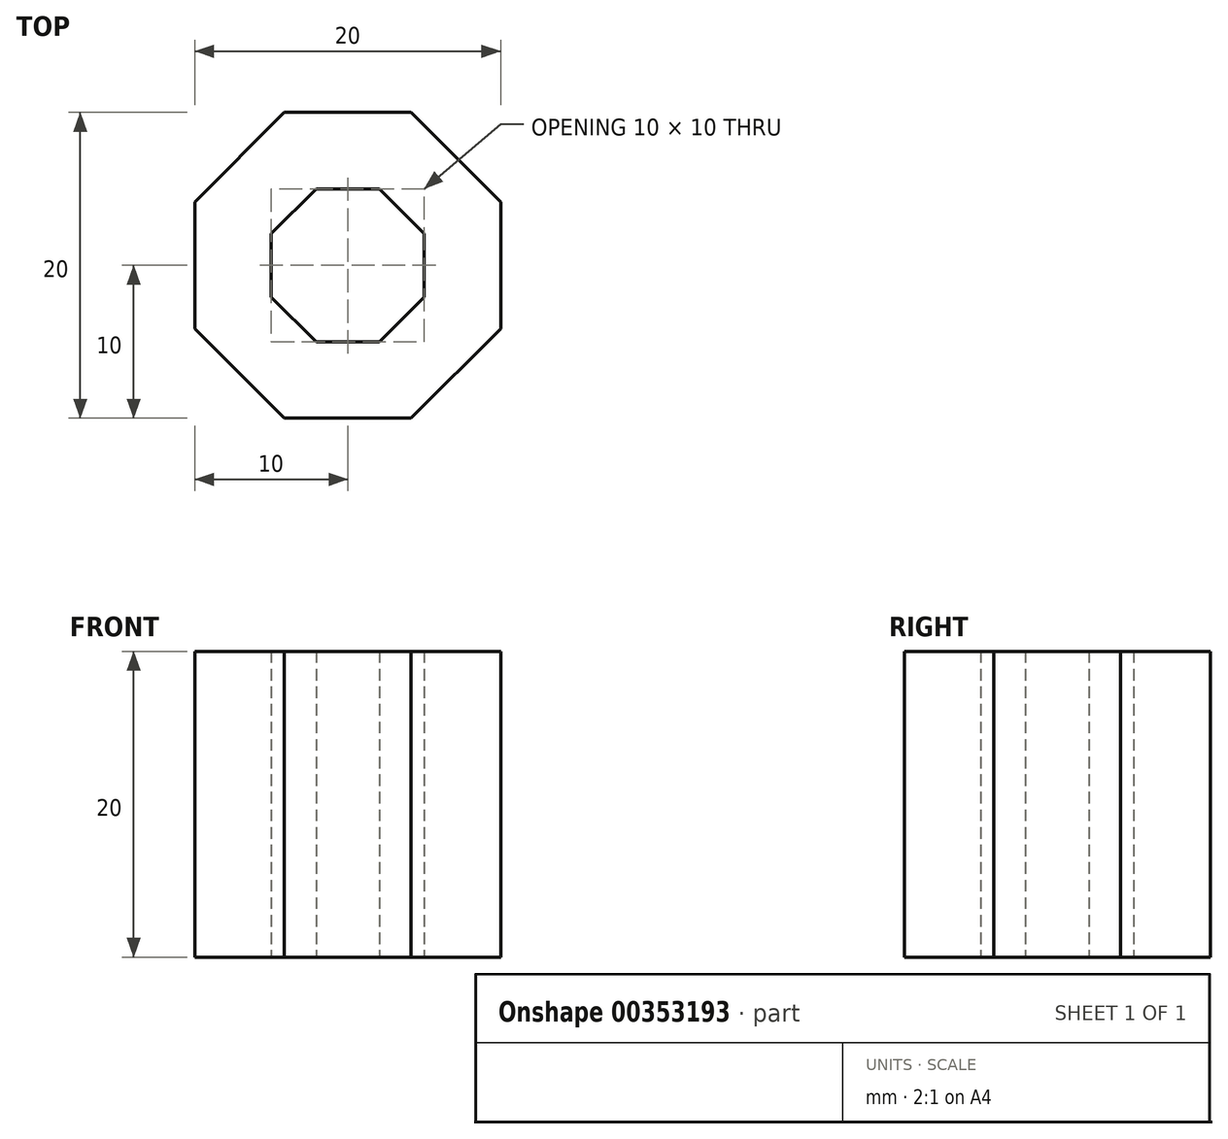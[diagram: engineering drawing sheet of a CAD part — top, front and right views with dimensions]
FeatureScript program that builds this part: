
annotation { "Feature Type Name" : "Feature", "Feature Type Description" : "" }
export const myFeature = defineFeature(function(context is Context, id is Id, definition is map)
    precondition{}
    {
        {
            var Q0;
            Q0=qCreatedBy(makeId("Top.planeOp"),FACE);
            var sketch = newSketch(context, id + "F0", { "sketchPlane" : qUnion([Q0])});
            skCircle(sketch, "E0", {"center": v(0, 0) * mm, "radius": 10 * mm});
            skCircle(sketch, "E1", {"center": v(0, 0) * mm, "radius": 5 * mm});
            skSolve(sketch);
        }
        {
            var Q0;
            Q0=qCreatedBy(makeId("Top.planeOp"),FACE);
            var sketch = newSketch(context, id + "F1", { "sketchPlane" : qUnion([Q0])});
            skCircle(sketch, "E2.cCircle", {"center": v(0, 0) * mm, "radius": 10 * mm, "construction": true});
            skLineSegment(sketch, "E2.0", {"start": v(-4.14, 10) * mm, "end": v(4.14, 10) * mm});
            skLineSegment(sketch, "E2.1", {"start": v(4.14, 10) * mm, "end": v(10, 4.14) * mm});
            skLineSegment(sketch, "E2.2", {"start": v(10, 4.14) * mm, "end": v(10, -4.14) * mm});
            skLineSegment(sketch, "E2.3", {"start": v(10, -4.14) * mm, "end": v(4.14, -10) * mm});
            skLineSegment(sketch, "E2.4", {"start": v(4.14, -10) * mm, "end": v(-4.14, -10) * mm});
            skLineSegment(sketch, "E2.5", {"start": v(-4.14, -10) * mm, "end": v(-10, -4.14) * mm});
            skLineSegment(sketch, "E2.6", {"start": v(-10, -4.14) * mm, "end": v(-10, 4.14) * mm});
            skLineSegment(sketch, "E2.7", {"start": v(-10, 4.14) * mm, "end": v(-4.14, 10) * mm});
            skPoint(sketch, "E2.0.midPoint", {"position": v(0, 10) * mm});
            skCircle(sketch, "E3.cCircle", {"center": v(0, 0) * mm, "radius": 5 * mm, "construction": true});
            skLineSegment(sketch, "E3.0", {"start": v(-2.07, 5) * mm, "end": v(2.07, 5) * mm});
            skLineSegment(sketch, "E3.1", {"start": v(2.07, 5) * mm, "end": v(5, 2.07) * mm});
            skLineSegment(sketch, "E3.2", {"start": v(5, 2.07) * mm, "end": v(5, -2.07) * mm});
            skLineSegment(sketch, "E3.3", {"start": v(5, -2.07) * mm, "end": v(2.07, -5) * mm});
            skLineSegment(sketch, "E3.4", {"start": v(2.07, -5) * mm, "end": v(-2.07, -5) * mm});
            skLineSegment(sketch, "E3.5", {"start": v(-2.07, -5) * mm, "end": v(-5, -2.07) * mm});
            skLineSegment(sketch, "E3.6", {"start": v(-5, -2.07) * mm, "end": v(-5, 2.07) * mm});
            skLineSegment(sketch, "E3.7", {"start": v(-5, 2.07) * mm, "end": v(-2.07, 5) * mm});
            skPoint(sketch, "E3.0.midPoint", {"position": v(0, 5) * mm});
            skSolve(sketch);
        }
        {
            var Q0;
            Q0=makeQuery(id+"F1.imprint","IMPRINT",FACE,{"disambiguationData":[TD([[makeQuery(id+"F1.imprint","IMPRINT",EDGE,{"derivedFrom":sQuery(id+"F1.wireOp",EDGE,"E2.0")}),-1.0]])]});
            extrude(context, id + "F2", {"entities" : qUnion([Q0]), "depth" : 20 * mm});
        }
    });
